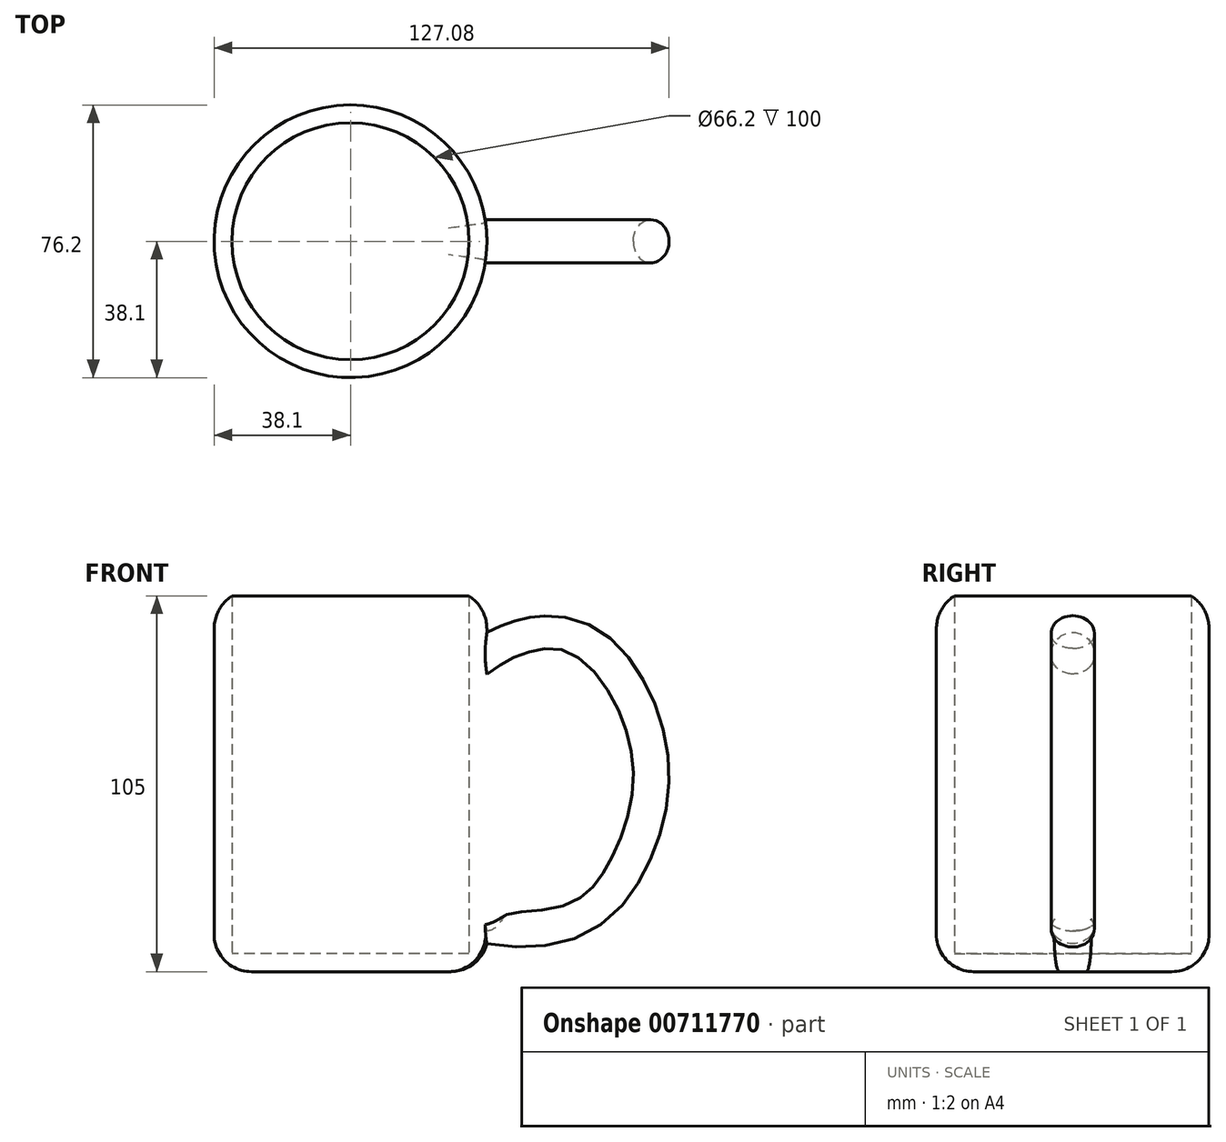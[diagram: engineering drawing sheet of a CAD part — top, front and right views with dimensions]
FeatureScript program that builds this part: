
annotation { "Feature Type Name" : "Feature", "Feature Type Description" : "" }
export const myFeature = defineFeature(function(context is Context, id is Id, definition is map)
    precondition{}
    {
        {
            var Q0;
            Q0=qCreatedBy(makeId("Top.planeOp"),FACE);
            var sketch = newSketch(context, id + "F0", { "sketchPlane" : qUnion([Q0])});
            skCircle(sketch, "E0", {"center": v(0, 0) * mm, "radius": 38.1 * mm});
            skSolve(sketch);
        }
        {
            var Q0;
            Q0 = qSketchRegion(id + "F0", true);
            extrude(context, id + "F1", {"entities" : qUnion([Q0]), "depth" : 105 * mm, "offsetDistance" : 25.4 * mm});
        }
        {
            var Q0;
            Q0=qCreatedBy(makeId("Front.planeOp"),FACE);
            var sketch = newSketch(context, id + "F2", { "sketchPlane" : qUnion([Q0])});
            skFitSpline(sketch, "E1", {"points": [v(35.18, 86.93) * mm, v(48.94, 93.22) * mm, v(65.84, 91.25) * mm, v(80.78, 70.42) * mm, v(82.35, 44.08) * mm, v(70.56, 20.89) * mm, v(53.26, 12.63) * mm, v(34, 15.38) * mm, v(33.22, 20.1) * mm], "startDerivative": vector(115.02, 66.78) * mm, "endDerivative": vector(12.92, 80.39) * mm});
            skSolve(sketch);
        }
        {
            var Q0;
            Q0=qCreatedBy(makeId("Right.planeOp"),FACE);
            cPlane(context, id + "F3", {"entities" : qUnion([Q0]), "cplaneType" : CPlaneType.OFFSET, "offset" : 32 * mm, "width" : 152.4 * mm, "height" : 152.4 * mm});
        }
        {
            var Q0;
            Q0=qCreatedBy(id+"F3.planeOp",FACE);
            var sketch = newSketch(context, id + "F4", { "sketchPlane" : qUnion([Q0])});
            skCircle(sketch, "E2", {"center": v(0, 85.34) * mm, "radius": 6.06 * mm});
            skSolve(sketch);
        }
        {
            var Q0;
            Q0 = qSketchRegion(id + "F4", true);
            var Q1;
            Q1=sQuery(id+"F2.wireOp",EDGE,"E1");
            sweep(context, id + "F5", {"operationType" : NewBodyOperationType.ADD, "profiles" : qUnion([Q0]), "path" : qUnion([Q1])});
        }
        {
            var Q0;
            Q0=makeQuery(id+"F1.opExtrude","CAP_FACE",FACE,{"disambiguationData":[OSD([sQuery(id+"F0.wireOp",EDGE,"E0")])],"isStart":false});
            shell(context, id + "F6", {"entities" : qUnion([Q0]), "thickness" : 5 * mm});
        }
        {
            var Q0;
            Q0=makeQuery(id+"F1.opExtrude","CAP_EDGE",EDGE,{"disambiguationData":[OSD([sQuery(id+"F0.wireOp",EDGE,"E0")])],"isStart":false});
            fillet(context, id + "F7", {"entities" : qUnion([Q0]), "radius" : 11.04 * mm, "tangentPropagation" : true, "allowEdgeOverflow" : false});
        }
        {
            var Q0;
            Q0=makeQuery(id+"F1.opExtrude","CAP_EDGE",EDGE,{"disambiguationData":[OSD([sQuery(id+"F0.wireOp",EDGE,"E0")])],"isStart":true});
            fillet(context, id + "F8", {"entities" : qUnion([Q0]), "radius" : 10.42 * mm, "tangentPropagation" : true, "allowEdgeOverflow" : false});
        }
    });
